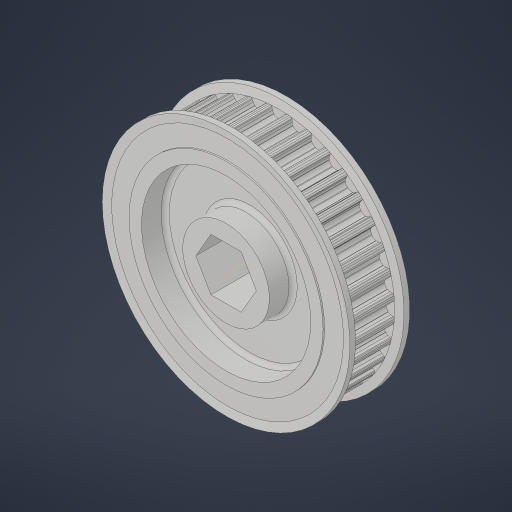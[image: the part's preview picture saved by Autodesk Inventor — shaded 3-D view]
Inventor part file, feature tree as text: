
AUTODESK INVENTOR PART (.ipt)
format: ipt  version: 2023.4 (Build 274418000, 418)  size: 879,104 bytes
history: native  units: in
note: dims shown in document units (in); Inventor stores cm internally (conversion verified against a paired STEP export)
features: mirror x1
ambient origin geometry x8: Origin, YZ Plane, XZ Plane, XY Plane, X Axis, Y Axis, Z Axis, Center Point
bodies: Solid1 (feature_tree)
feature tree (1):
  mirror  "Mirror1"
